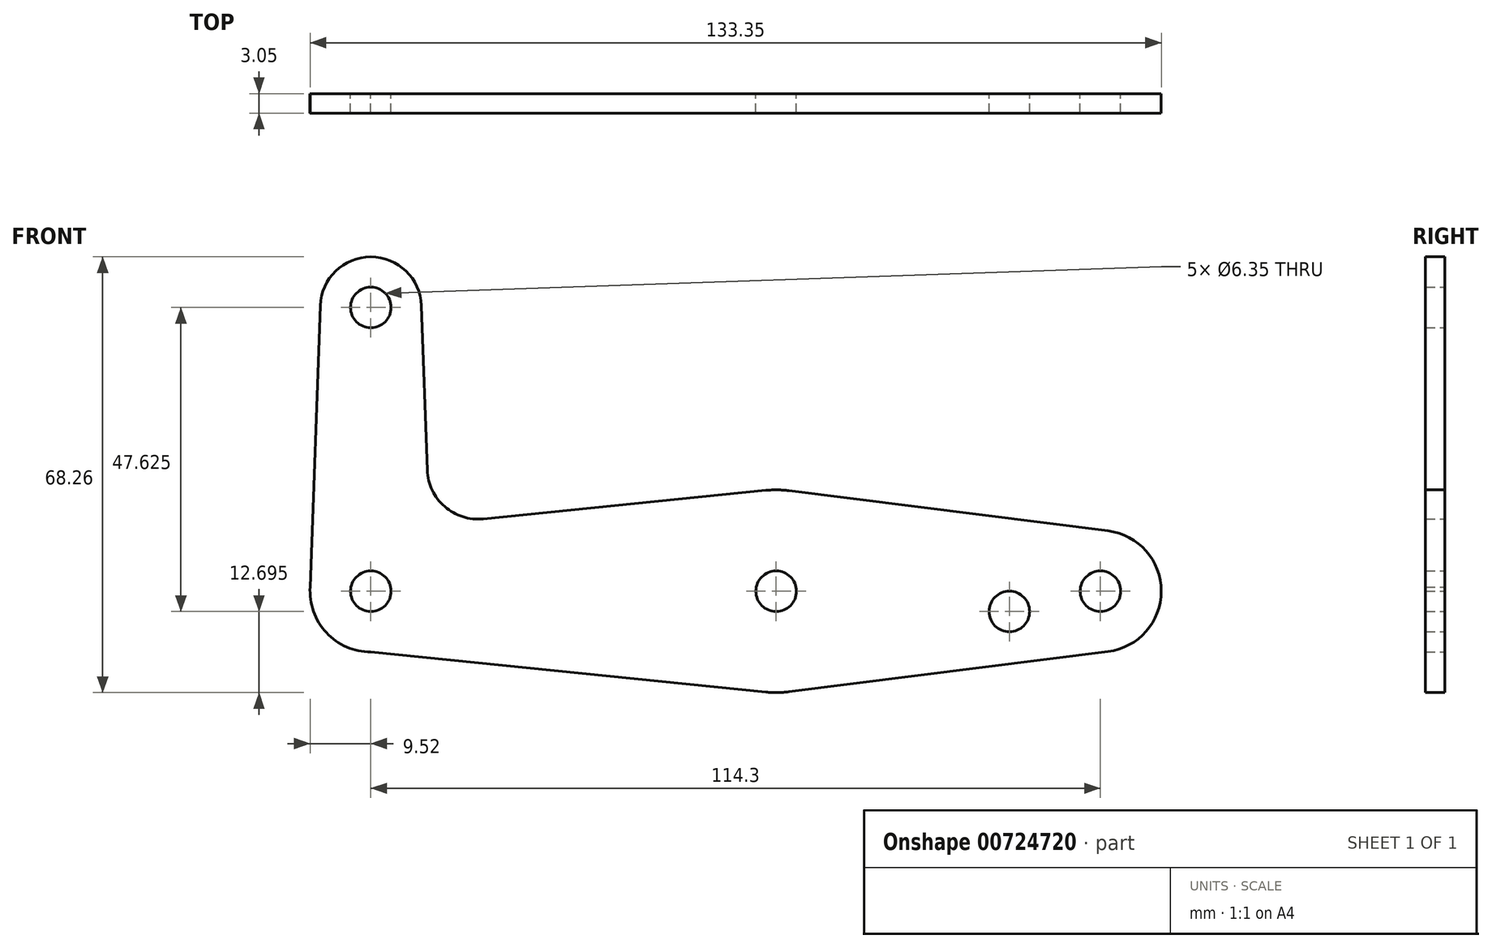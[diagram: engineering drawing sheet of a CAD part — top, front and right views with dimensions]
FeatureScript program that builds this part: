
annotation { "Feature Type Name" : "Feature", "Feature Type Description" : "" }
export const myFeature = defineFeature(function(context is Context, id is Id, definition is map)
    precondition{}
    {
        {
            var Q0;
            Q0=qCreatedBy(makeId("Front.planeOp"),FACE);
            var sketch = newSketch(context, id + "F0", { "sketchPlane" : qUnion([Q0])});
            skLineSegment(sketch, "E0", {"start": v(0, 0) * mm, "end": v(114.3, 0) * mm, "construction": true});
            skLineSegment(sketch, "E1", {"start": v(0, 0) * mm, "end": v(0, 44.45) * mm, "construction": true});
            skCircle(sketch, "E2", {"center": v(0, 44.45) * mm, "radius": 7.94 * mm});
            skCircle(sketch, "E3", {"center": v(0, 0) * mm, "radius": 9.53 * mm});
            skCircle(sketch, "E4", {"center": v(114.3, 0) * mm, "radius": 9.53 * mm});
            skCircle(sketch, "E5", {"center": v(63.5, 0) * mm, "radius": 15.88 * mm});
            skLineSegment(sketch, "E6", {"start": v(115.5, 9.45) * mm, "end": v(65.48, 15.75) * mm});
            skLineSegment(sketch, "E7", {"start": v(0, -9.53) * mm, "end": v(61.9, -15.8) * mm});
            skLineSegment(sketch, "E8", {"start": v(65.48, -15.75) * mm, "end": v(115.5, -9.45) * mm});
            skLineSegment(sketch, "E9", {"start": v(-9.53, 0) * mm, "end": v(-7.93, 44.73) * mm});
            skCircle(sketch, "E10", {"center": v(114.3, 0) * mm, "radius": 3.18 * mm});
            skCircle(sketch, "E11", {"center": v(63.5, 0) * mm, "radius": 3.18 * mm});
            skCircle(sketch, "E12", {"center": v(0, 0) * mm, "radius": 3.18 * mm});
            skCircle(sketch, "E13", {"center": v(0, 44.45) * mm, "radius": 3.18 * mm});
            skLineSegment(sketch, "E14", {"start": v(17.6, 11.34) * mm, "end": v(61.91, 15.8) * mm});
            skLineSegment(sketch, "E15", {"start": v(7.93, 44.73) * mm, "end": v(8.85, 18.97) * mm});
            skPoint(sketch, "E16.newPointA", {"position": v(9.53, 0) * mm});
            skArc(sketch, "E16.filletArc", {"start": v(8.85, 18.97) * mm, "mid": v(11.57, 13.26) * mm, "end": v(17.6, 11.34) * mm});
            skCircle(sketch, "E17", {"center": v(100.03, -3.18) * mm, "radius": 3.18 * mm});
            skSolve(sketch);
        }
        {
            var Q0;
            Q0 = qSketchRegion(id + "F0", true);
            extrude(context, id + "F1", {"entities" : qUnion([Q0]), "depth" : 3.05 * mm, "offsetDistance" : 25.4 * mm});
        }
    });
